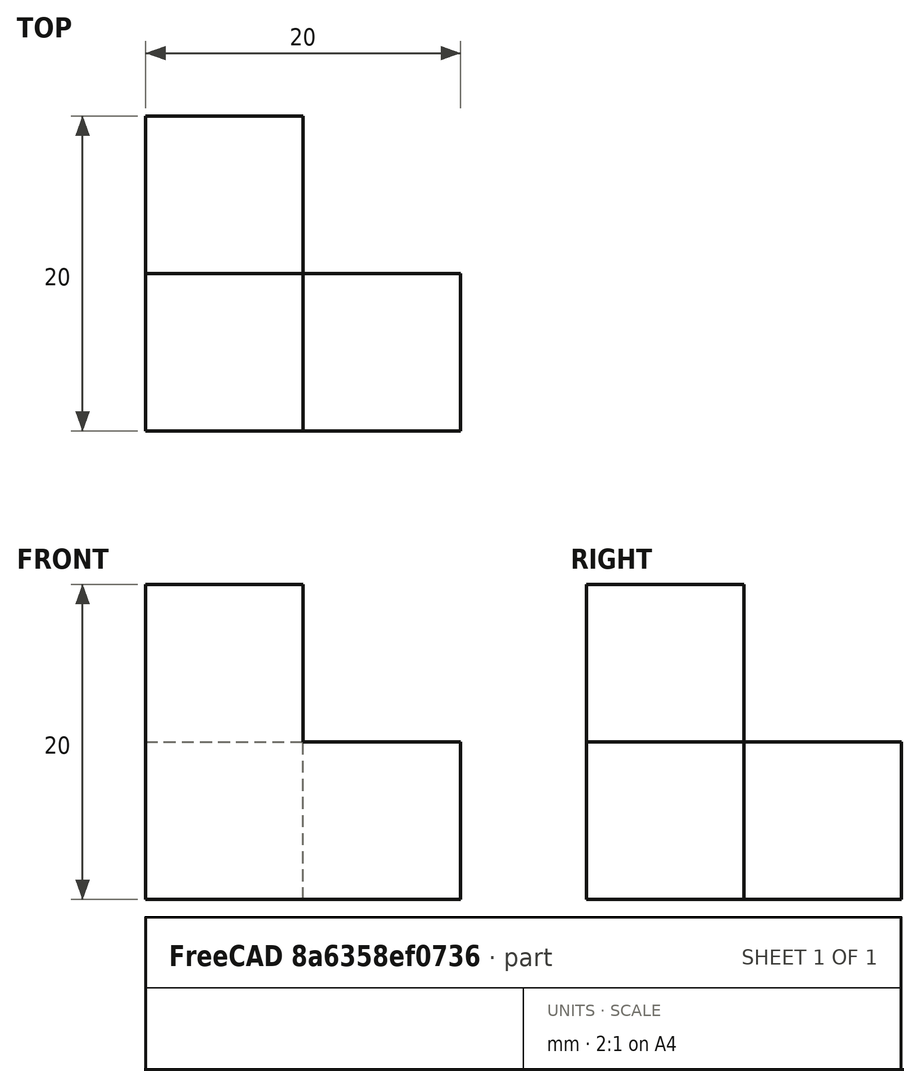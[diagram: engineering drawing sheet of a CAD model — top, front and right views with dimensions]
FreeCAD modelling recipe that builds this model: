
FCSTD DOCUMENT  (FreeCAD 0.21R33771 (Git))
Label: OJT1_T05R01_unions_qubert2
License: All rights reserved
LicenseURL: http://en.wikipedia.org/wiki/All_rights_reserved
objects: Part::Box×4, Part::MultiFuse×1
note: 5 computed .brp shape members not serialized (recipe doc carries the construction recipe); baked Part::Feature solids carry a one-line shape summary decoded from their .brp

FEATURE [Part::Box] Box  label="nivell1_cub1"
  AttacherType = Attacher::AttachEngine3D
  Height = 10
  Length = 10
  Width = 10
FEATURE [Part::Box] Box001  label="nivell1_cub2"
  AttacherType = Attacher::AttachEngine3D
  Height = 10
  Length = 10
  Placement = pos=(10,0,0) rot=(0,0,1;0rad)
  Width = 10
FEATURE [Part::Box] Box002  label="nivell1_cub3"
  AttacherType = Attacher::AttachEngine3D
  Height = 10
  Length = 10
  Placement = pos=(0,10,0) rot=(0,0,1;0rad)
  Width = 10
FEATURE [Part::Box] Box003  label="nivell2_cub1"
  AttacherType = Attacher::AttachEngine3D
  Height = 10
  Length = 10
  Placement = pos=(0,0,10) rot=(0,0,1;0rad)
  Width = 10
FEATURE [Part::MultiFuse] Fusion
  Refine = true
  Shapes = -> [Box,Box001,Box002,Box003]
